# Revit family: Door-NanaWall-HSW-60_Concept_3
name_source: partatom
category: Doors
revit_build: Autodesk Revit Architecture 2013 (Build: 20130531_2115(x64)
units: mm (PartAtom-declared; Revit-internal decimal feet)

## types (1)
- Standard
    04 CSI = 08 41 13
    95 CSI = 8411
    Assembly Code = B2030110
    Cost Info = http://www.nanawall.com
    Description = Thermally Broken Aluminum Framed Sign Track Sliding System
    Engineering Details URL = http://www.nanawall.com
    Exterior Wall Offset = 0' - 9 17/32"
    Filler = Rubber - NanaWall - Black
    Function = Interior
    Glass Material = Glass - NanaWall - Generic
    Glazing Options = http://www.nanawall.com
    Height = 10' - 0"
    Height Constraint = 10' - 0"
    Installation and Service URL = http://www.nanawall.com
    Jamb Height = 9' - 2 47/64"
    Manufacturer = NanaWall Systems, Inc.
    Manufacturer Fax = (415) 383-0312
    Max Panel Height = 9' - 2 21/32"
    Model = HSW-60
    Opening Width = 11' - 3 17/64"
    Panel Height = 9' - 2 21/32"
    Performance URL = http://www.nanawall.com
    Product Page URL = http://www.nanawall.com
    Rough Height = 9' - 9 73/256"
    Rough Width = 11' - 8 115/128"
    Sash = Metal - NanaWall - Aluminum
    Sill Width = 11' - 2 15/128"
    Sills Available = Raised, Low Profile Saddle, Flush
    Size Note = Adjust Height and Width as necessary to fit your project needs. Multiple Panel and opening configurations are available. See Product Page URL for more information.
    Stack Offset = 0' - 8"
    Subcategory = Folding Door
    Thickness = 0' - 2 21/64"
    U Value = 0.26
    URL = http://www.nanawall.com
    Wall Closure = By host
    Warranty URL = http://www.nanawall.com
    Width = 12' - 0"

## geometry (parser evidence)
native form markers: Blend x4, Sweep x31
no freeform markers — native parametric forms only
